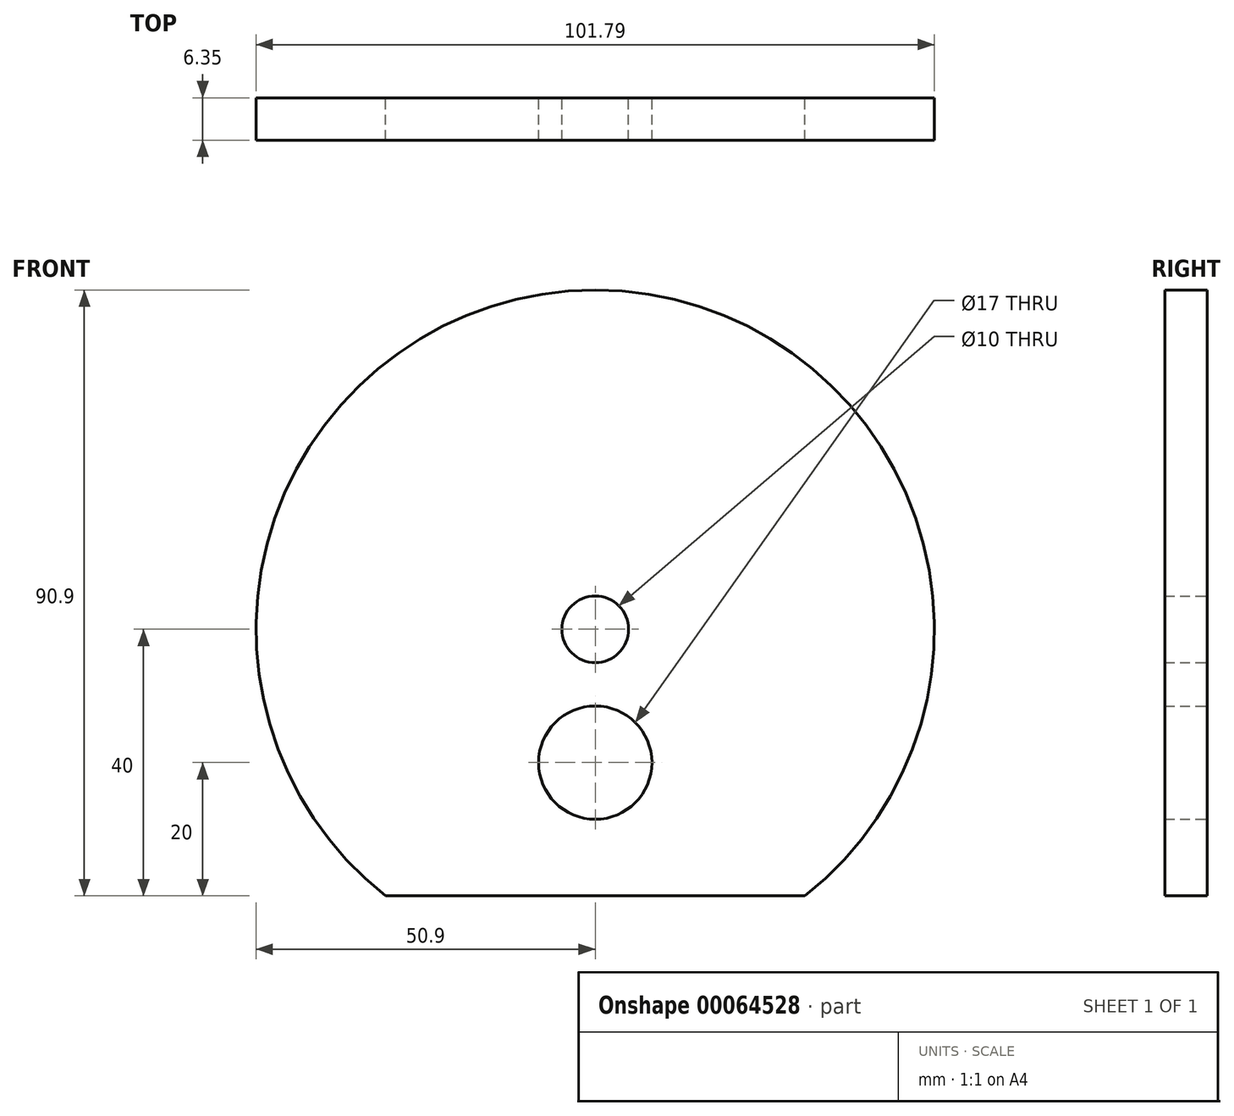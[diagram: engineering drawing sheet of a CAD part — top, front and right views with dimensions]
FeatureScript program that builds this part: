
annotation { "Feature Type Name" : "Feature", "Feature Type Description" : "" }
export const myFeature = defineFeature(function(context is Context, id is Id, definition is map)
    precondition{}
    {
        {
            var Q0;
            Q0=qCreatedBy(makeId("Front.planeOp"),FACE);
            var sketch = newSketch(context, id + "F0", { "sketchPlane" : qUnion([Q0])});
            skCircle(sketch, "E0", {"center": v(0, 0) * mm, "radius": 40 * mm});
            skCircle(sketch, "E1", {"center": v(0, 0) * mm, "radius": 50.9 * mm});
            skLineSegment(sketch, "E2.bottom", {"start": v(-67.09, -40) * mm, "end": v(71.88, -40) * mm});
            skLineSegment(sketch, "E2.top", {"start": v(-67.09, -62.36) * mm, "end": v(71.88, -62.36) * mm});
            skLineSegment(sketch, "E2.left", {"start": v(-67.09, -40) * mm, "end": v(-67.09, -62.36) * mm});
            skLineSegment(sketch, "E2.right", {"start": v(71.88, -40) * mm, "end": v(71.88, -62.36) * mm});
            skCircle(sketch, "E3", {"center": v(0, 0) * mm, "radius": 5 * mm});
            skCircle(sketch, "E4", {"center": v(0, -20) * mm, "radius": 8.5 * mm});
            skSolve(sketch);
        }
        {
            var Q0;
            Q0=makeQuery(id+"F0.imprint","IMPRINT",FACE,{"disambiguationData":[TD([[makeQuery(id+"F0.imprint","IMPRINT",EDGE,{"derivedFrom":sQuery(id+"F0.wireOp",EDGE,"E0")}),1.0]])]});
            var Q1;
            Q1=makeQuery(id+"F0.imprint","IMPRINT",FACE,{"disambiguationData":[TD([[makeQuery(id+"F0.imprint","IMPRINT",EDGE,{"derivedFrom":sQuery(id+"F0.wireOp",EDGE,"E0")}),-1.0]])]});
            extrude(context, id + "F1", {"entities" : qUnion([Q0, Q1]), "depth" : 6.35 * mm});
        }
    });
